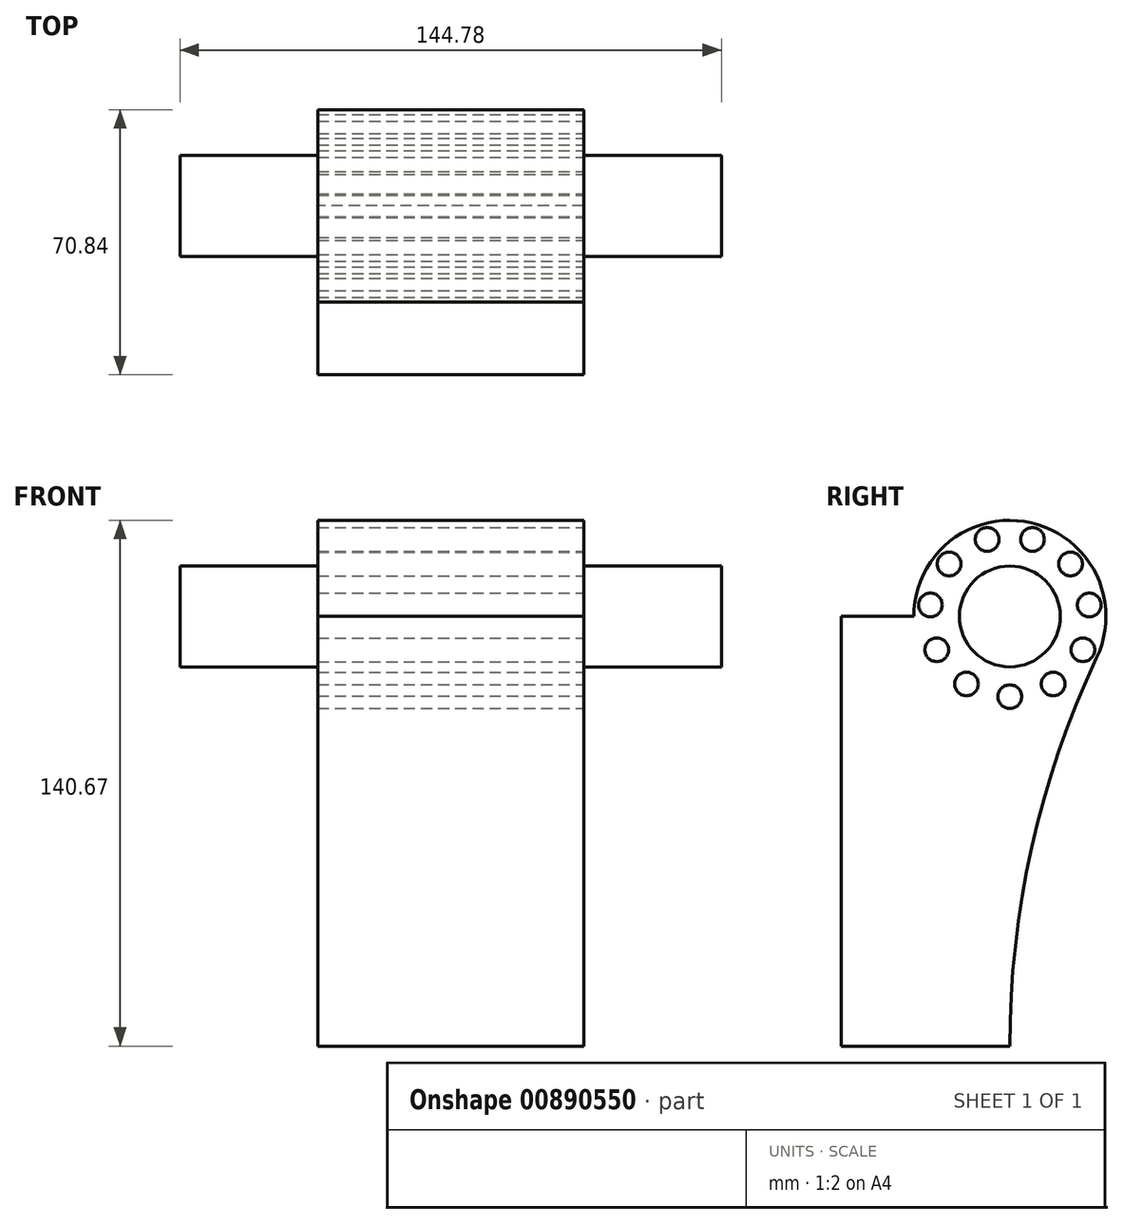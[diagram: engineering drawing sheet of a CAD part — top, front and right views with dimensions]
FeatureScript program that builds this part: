
annotation { "Feature Type Name" : "Feature", "Feature Type Description" : "" }
export const myFeature = defineFeature(function(context is Context, id is Id, definition is map)
    precondition{}
    {
        {
            var Q0;
            Q0=qCreatedBy(makeId("Right.planeOp"),FACE);
            var sketch = newSketch(context, id + "F0", { "sketchPlane" : qUnion([Q0])});
            skLineSegment(sketch, "E0.bottom", {"start": v(22.57, 57.48) * mm, "end": v(-22.57, 57.48) * mm});
            skLineSegment(sketch, "E0.top", {"start": v(22.57, -57.48) * mm, "end": v(-22.57, -57.48) * mm});
            skLineSegment(sketch, "E0.left", {"start": v(22.57, 57.48) * mm, "end": v(22.57, -57.48) * mm});
            skLineSegment(sketch, "E0.right", {"start": v(-22.57, 57.48) * mm, "end": v(-22.57, -57.48) * mm});
            skPoint(sketch, "E0.middle", {"position": v(0, 0) * mm});
            skCircle(sketch, "E1", {"center": v(22.57, 57.48) * mm, "radius": 25.7 * mm});
            skCircle(sketch, "E2", {"center": v(22.57, 57.48) * mm, "radius": 13.48 * mm});
            skArc(sketch, "E3", {"start": v(45.92, 46.73) * mm, "mid": v(28.47, -4.09) * mm, "end": v(22.57, -57.48) * mm});
            skSolve(sketch);
        }
        {
            var Q0;
            {var subQ0=sQuery(id+"F0.wireOp",EDGE,"E3");var subQ3=sQuery(id+"F0.wireOp",EDGE,"E1");var subQ5=makeQuery(id+"F0.imprint","INTERSECT",VERTEX,{"disambiguationData":[OD(1.0)],"derivedFrom":[subQ3,subQ0]});Q0=makeQuery(id+"F0.imprint","IMPRINT",FACE,{"disambiguationData":[TD([[makeQuery(id+"F0.imprint","IMPRINT",EDGE,{"disambiguationData":[TD([[subQ5,1.0]])],"derivedFrom":subQ3}),-1.0]])]});}
            var Q1;
            {var subQ1=sQuery(id+"F0.wireOp",EDGE,"E1");var subQ8=sQuery(id+"F0.wireOp",EDGE,"E0.bottom");var subQ9=makeQuery(id+"F0.imprint","INTERSECT",VERTEX,{"derivedFrom":[subQ8,subQ1]});Q1=makeQuery(id+"F0.imprint","IMPRINT",FACE,{"disambiguationData":[TD([[makeQuery(id+"F0.imprint","IMPRINT",EDGE,{"disambiguationData":[TD([[subQ9,1.0]])],"derivedFrom":subQ8}),-1.0]])]});}
            var Q2;
            {var subQ0=sQuery(id+"F0.wireOp",EDGE,"E1");var subQ1=sQuery(id+"F0.wireOp",EDGE,"E0.bottom");var subQ2=makeQuery(id+"F0.imprint","INTERSECT",VERTEX,{"derivedFrom":[subQ1,subQ0]});Q2=makeQuery(id+"F0.imprint","IMPRINT",FACE,{"disambiguationData":[TD([[makeQuery(id+"F0.imprint","IMPRINT",EDGE,{"disambiguationData":[TD([[subQ2,1.0]])],"derivedFrom":subQ1}),1.0]])]});}
            var Q3;
            {var subQ1=sQuery(id+"F0.wireOp",EDGE,"E0.top");Q3=makeQuery(id+"F0.imprint","IMPRINT",FACE,{"disambiguationData":[TD([[makeQuery(id+"F0.imprint","IMPRINT",EDGE,{"derivedFrom":subQ1}),-1.0]])]});}
            extrude(context, id + "F1", {"entities" : qUnion([Q0, Q1, Q2, Q3]), "depth" : 9.9 * mm, "offsetDistance" : 25.4 * mm});
        }
        {
            var Q0;
            Q0 = qSketchRegion(id + "F0", true);
            extrude(context, id + "F2", {"entities" : qUnion([Q0]), "endBound" : BoundingType.SYMMETRIC, "oppositeDirection" : true, "depth" : 71.12 * mm, "offsetDistance" : 25.4 * mm});
        }
        {
            var Q0;
            Q0=makeQuery(id+"F2.opExtrude","CAP_FACE",FACE,{"disambiguationData":[OSD([sQuery(id+"F0.wireOp",EDGE,"E0.bottom"),sQuery(id+"F0.wireOp",EDGE,"E0.top"),sQuery(id+"F0.wireOp",EDGE,"E0.right"),sQuery(id+"F0.wireOp",EDGE,"E1"),sQuery(id+"F0.wireOp",EDGE,"E2"),sQuery(id+"F0.wireOp",EDGE,"E3")])],"isStart":true});
            var sketch = newSketch(context, id + "F3", { "sketchPlane" : qUnion([Q0])});
            skLineSegment(sketch, "E4.0", {"start": v(22.57, 57.48) * mm, "end": v(22.57, -57.48) * mm, "construction": true});
            skPoint(sketch, "E5", {"position": v(22.57, 36.02) * mm});
            skPoint(sketch, "E6.1.0", {"position": v(34.17, 39.43) * mm});
            skPoint(sketch, "E6.2.0", {"position": v(42.1, 48.57) * mm});
            skPoint(sketch, "E6.3.0", {"position": v(43.81, 60.54) * mm});
            skPoint(sketch, "E6.4.0", {"position": v(38.79, 71.54) * mm});
            skPoint(sketch, "E6.5.0", {"position": v(28.61, 78.08) * mm});
            skPoint(sketch, "E6.6.0", {"position": v(16.52, 78.08) * mm});
            skPoint(sketch, "E6.7.0", {"position": v(6.34, 71.54) * mm});
            skPoint(sketch, "E6.8.0", {"position": v(1.32, 60.54) * mm});
            skPoint(sketch, "E6.9.0", {"position": v(3.04, 48.57) * mm});
            skPoint(sketch, "E6.10.0", {"position": v(10.96, 39.43) * mm});
            skPoint(sketch, "E6.center", {"position": v(22.57, 57.48) * mm});
            skSolve(sketch);
        }
        {
            var Q0;
            Q0=sQuery(id+"F3.wireOp",VERTEX,"E6.4.0");
            var Q1;
            Q1=sQuery(id+"F3.wireOp",VERTEX,"E6.3.0");
            var Q2;
            Q2=sQuery(id+"F3.wireOp",VERTEX,"E6.2.0");
            var Q3;
            Q3=sQuery(id+"F3.wireOp",VERTEX,"E5");
            var Q4;
            Q4=sQuery(id+"F3.wireOp",VERTEX,"E6.10.0");
            var Q5;
            Q5=sQuery(id+"F3.wireOp",VERTEX,"E6.1.0");
            var Q6;
            Q6=sQuery(id+"F3.wireOp",VERTEX,"E6.9.0");
            var Q7;
            Q7=sQuery(id+"F3.wireOp",VERTEX,"E6.8.0");
            var Q8;
            Q8=sQuery(id+"F3.wireOp",VERTEX,"E6.7.0");
            var Q9;
            Q9=sQuery(id+"F3.wireOp",VERTEX,"E6.6.0");
            var Q10;
            Q10=sQuery(id+"F3.wireOp",VERTEX,"E6.5.0");
            var Q11;
            Q11=makeQuery(id+"F1.opExtrude","SWEPT_BODY",BODY,{"disambiguationData":[OSD([sQuery(id+"F0.wireOp",EDGE,"E0.bottom"),sQuery(id+"F0.wireOp",EDGE,"E0.top"),sQuery(id+"F0.wireOp",EDGE,"E0.right"),sQuery(id+"F0.wireOp",EDGE,"E1"),sQuery(id+"F0.wireOp",EDGE,"E2"),sQuery(id+"F0.wireOp",EDGE,"E3")])]});
            var Q12;
            Q12=makeQuery(id+"F2.opExtrude","SWEPT_BODY",BODY,{"disambiguationData":[OSD([sQuery(id+"F0.wireOp",EDGE,"E0.bottom"),sQuery(id+"F0.wireOp",EDGE,"E0.top"),sQuery(id+"F0.wireOp",EDGE,"E0.right"),sQuery(id+"F0.wireOp",EDGE,"E1"),sQuery(id+"F0.wireOp",EDGE,"E2"),sQuery(id+"F0.wireOp",EDGE,"E3")])]});
            hole(context, id + "F4", {"style" : HoleStyle.SIMPLE, "endStyle" : HoleEndStyle.THROUGH, "holeDiameter" : 6.35 * mm, "majorDiameter" : 6.35 * mm, "isTappedThrough" : true, "tappedDepth" : 12.7 * mm, "tapClearance" : 3, "locations" : qUnion([Q0, Q1, Q2, Q3, Q4, Q5, Q6, Q7, Q8, Q9, Q10]), "scope" : qUnion([Q11, Q12])});
        }
        {
            var Q0;
            {var subQ0=sQuery(id+"F0.wireOp",EDGE,"E0.left");var subQ1=sQuery(id+"F0.wireOp",EDGE,"E0.bottom");var subQ2=makeQuery(id+"F0.imprint","INTERSECT",VERTEX,{"derivedFrom":[subQ1,subQ0]});Q0=makeQuery(id+"F0.imprint","IMPRINT",FACE,{"disambiguationData":[TD([[makeQuery(id+"F0.imprint","IMPRINT",EDGE,{"disambiguationData":[TD([[subQ2,-1.0]])],"derivedFrom":subQ1}),-1.0]])]});}
            var Q1;
            {var subQ0=sQuery(id+"F0.wireOp",EDGE,"E0.left");var subQ1=sQuery(id+"F0.wireOp",EDGE,"E0.bottom");var subQ2=makeQuery(id+"F0.imprint","INTERSECT",VERTEX,{"derivedFrom":[subQ1,subQ0]});Q1=makeQuery(id+"F0.imprint","IMPRINT",FACE,{"disambiguationData":[TD([[makeQuery(id+"F0.imprint","IMPRINT",EDGE,{"disambiguationData":[TD([[subQ2,-1.0]])],"derivedFrom":subQ1}),1.0]])]});}
            extrude(context, id + "F5", {"entities" : qUnion([Q0, Q1]), "operationType" : NewBodyOperationType.ADD, "endBound" : BoundingType.SYMMETRIC, "oppositeDirection" : true, "depth" : 144.78 * mm, "offsetDistance" : 25.4 * mm});
        }
    });
